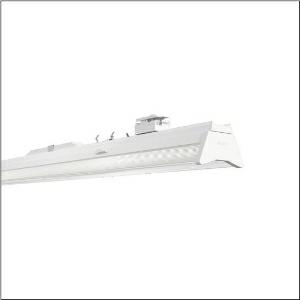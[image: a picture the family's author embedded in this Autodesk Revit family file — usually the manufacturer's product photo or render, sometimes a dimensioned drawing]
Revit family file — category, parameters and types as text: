
# Revit family: licross_11_performance_ho_51td16dn4fxm
name_source: partatom
category: Lighting Fixtures
units: mm (PartAtom-declared; Revit-internal decimal feet)

## family parameters
Cut with Voids When Loaded = No
Host = Face
Light Source = No
Part Type = Normal
Room Calculation Point = No
Round Connector Dimension = Use Diameter
Shared = No

## types (1)
- --- (1 x LED, 15460 lm, 87.3 W, 4000K)
    Apparent Load = 87 VA
    CIE Flux Codes = 63 87 95 78 100
    Color Rendering = 80
    Color Temperature = 4000K
    Default Elevation = 1800 mm
    Description = Licross 11 Performance HO, luminaire insert, of sheet steel, galvanised, coil coated, white, length: 1.500mm, width: 120mm, height: 123mm, LED rated luminous flux: 15.460lm, light colour: 840, SDCM (Standard Deviation of Colour Matching)MacAdam ≤ 2 SDCM (initial), control gear: DALI 2, with plug, 5-pole, with phase selection, mains connection: 220..240V, AC, 50/60Hz, rated input power: 87W, internal wiring halogen-free, primary light control with lens, of plastic, primary optical cover: cover, of PMMA, light emission: direct/indirect distribution, primary light characteristic: symmetric, protection rating (complete): IP54, insulation class (complete): insulation class I (protective earthing), certification: CE, ENEC, VDE, UKCA, protection symbol: D if used in an environment with non-conductive dust loads with corresponding accessories, impact resistance: IK06, permissible ambient temperature for indoor applications: -25..+30°C, corresponds to IFS (International Featured Standards) requirements for safety and quality in the food industry, reducing of maximum allowable ambient temperature of 5°C with ceiling mounting, LABS conformity tested according to VDMA 24364:2018-05, The light source and the operating device comply with the requirements of the Ecodesign Regulation (EU) 2019/2020 and are replaceable in accordance with this regulation, packaging unit: 1 piece
    Height = 114 mm
    Lamp = 1 x LED
    Lamp Light Flux = 15460 lm
    Lamp Power = 87.3 W
    Lamp count = 1
    Length = 1500 mm
    Luminous efficacy = 177 lm/W
    Manufacturer = Siteco
    ModVariant = No
    Model = 51TD16DN4FXM
    Mounting Place = Ceiling
    Mounting Type = Pendant
    Number of Poles = 1
    OnlyDefault = Yes
    Power Factor = 1
    Product Name = Licross 11 Performance HO
    Product group = luminaire insert | ceiling pendant
    ProductGroupID = 901
    Protection Class = Protection class I
    Protection Degree = IP 54
    RLX_Detail_Level = 1
    RLX_Emergency_Light_Flux = 0 lm
    RLX_Emergency_Type = 0
    RLX_Emergency_Type_DB = No
    RlxData = <blob elided: 34353 chars, md5=8fa5326b>
    Socket = socket
    Standby Power = 0 W
    System Light Flux = 15460 lm
    System Power = 87 W
    Type Comments = factory setting: luminous flux: 100 % | dim-lin: 254 | 589 mA
    Type Image = l_1256138.jpg
    URL = http://relux.com
    VarID = @adj_102935
    Voltage = 0 V
    Weight = 0.00 kg
    Width = 120 mm

## geometry (parser evidence)
native form markers: Blend x4, Sweep x13
no freeform markers — native parametric forms only
